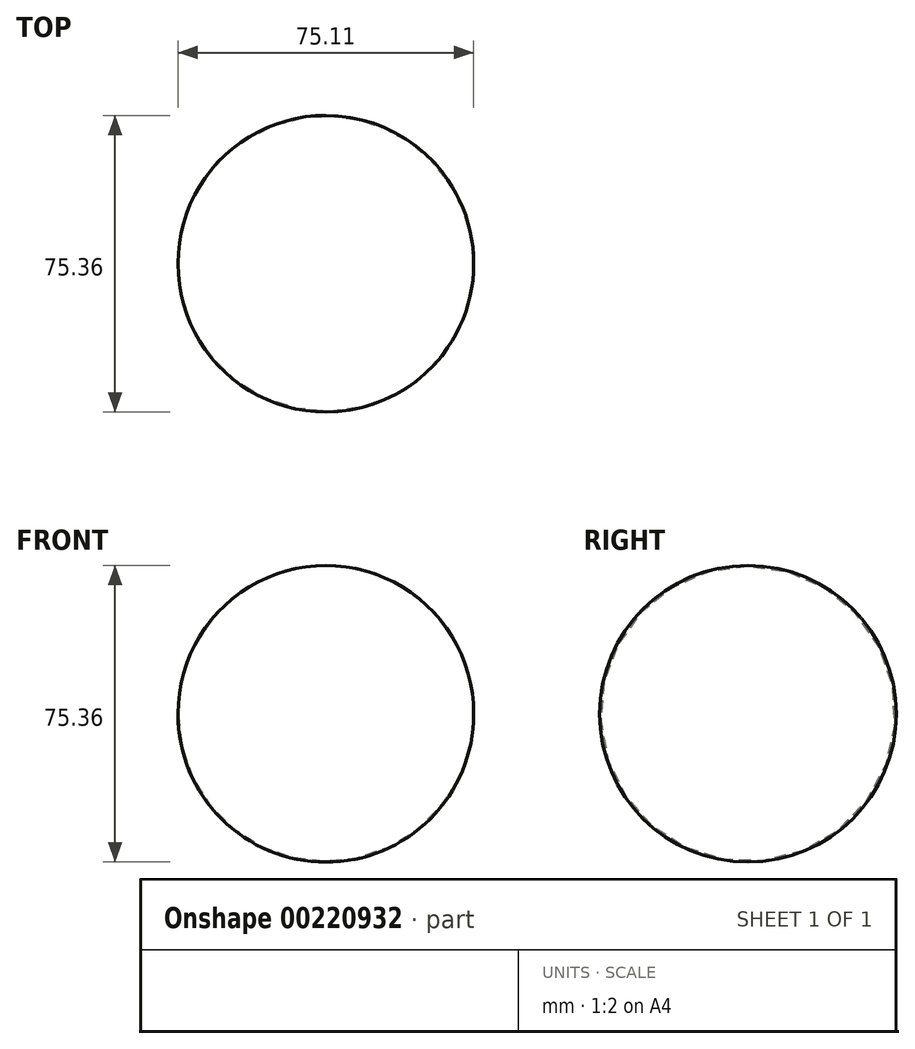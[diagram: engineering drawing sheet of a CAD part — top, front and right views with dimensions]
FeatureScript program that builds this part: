
annotation { "Feature Type Name" : "Feature", "Feature Type Description" : "" }
export const myFeature = defineFeature(function(context is Context, id is Id, definition is map)
    precondition{}
    {
        {
            var Q0;
            Q0=qCreatedBy(makeId("Front.planeOp"),FACE);
            var sketch = newSketch(context, id + "F0", { "sketchPlane" : qUnion([Q0])});
            skArc(sketch, "E0", {"start": v(-75.1, 0) * mm, "mid": v(-37.55, -37.68) * mm, "end": v(0, 0) * mm});
            skSolve(sketch);
        }
        {
            var Q0;
            Q0=qCreatedBy(makeId("Front.planeOp"),FACE);
            var sketch = newSketch(context, id + "F1", { "sketchPlane" : qUnion([Q0])});
            skLineSegment(sketch, "E1", {"start": v(-75.65, 0) * mm, "end": v(0, 0) * mm});
            skSolve(sketch);
        }
        {
            var Q0;
            Q0=sQuery(id+"F0.wireOp",EDGE,"E0");
            var Q1;
            Q1=sQuery(id+"F1.wireOp",EDGE,"E1");
            revolve(context, id + "F2", {"bodyType" : ToolBodyType.SURFACE, "surfaceEntities" : qUnion([Q0]), "axis" : qUnion([Q1]), "revolveType" : RevolveType.FULL});
        }
    });
